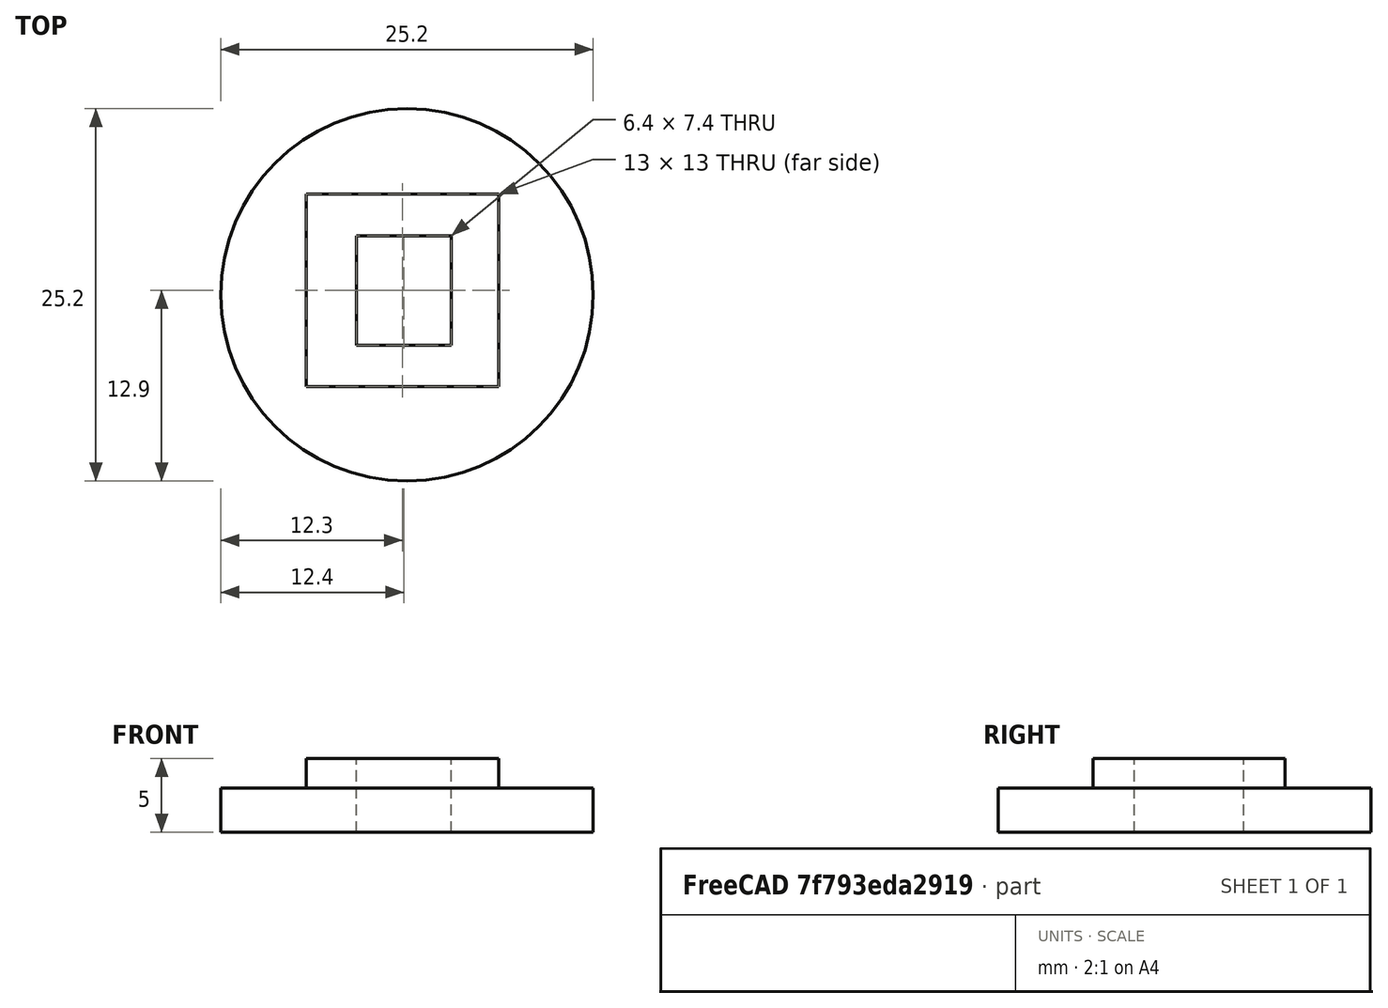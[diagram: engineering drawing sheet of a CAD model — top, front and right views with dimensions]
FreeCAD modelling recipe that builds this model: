
FCSTD DOCUMENT  (FreeCAD 0.21R33668 +26 (Git))
Label: fibre_holder
License: All rights reserved
LicenseURL: http://en.wikipedia.org/wiki/All_rights_reserved
objects: Part::Cylinder×4, Part::Box×2, Part::Cut×2, Part::MultiFuse×1, Part::MultiCommon×1
note: 10 computed .brp shape members not serialized (recipe doc carries the construction recipe); baked Part::Feature solids carry a one-line shape summary decoded from their .brp

FEATURE [Part::Box] Box  label="Cube"
  AttacherType = Attacher::AttachEngine3D
  Height = 10
  Length = 6.4
  Width = 7.4
FEATURE [Part::Cylinder] Cylinder
  Angle = 360
  AttacherType = Attacher::AttachEngine3D
  FirstAngle = 0
  Height = 10
  Placement = pos=(3.2,3.5,0) rot=(0,0,1;0rad)
  Radius = 17.4
  SecondAngle = 0
FEATURE [Part::Cylinder] Cylinder001
  Angle = 360
  AttacherType = Attacher::AttachEngine3D
  FirstAngle = 0
  Height = 12
  Placement = pos=(3.2,3.5,0) rot=(0,0,1;0rad)
  Radius = 14.4
  SecondAngle = 0
FEATURE [Part::Cylinder] Cylinder002
  Angle = 360
  AttacherType = Attacher::AttachEngine3D
  FirstAngle = 0
  Height = 3
  Placement = pos=(3.2,3.5,0) rot=(0,0,1;0rad)
  Radius = 15.4
  SecondAngle = 0
FEATURE [Part::Cut] Cut
  Base = -> Cylinder
  Tool = -> Cylinder001
FEATURE [Part::Box] Box001  label="Cube001"
  AttacherType = Attacher::AttachEngine3D
  Height = 5
  Length = 13
  Placement = pos=(-3.4,-2.8,0) rot=(0,0,1;0rad)
  Width = 13
FEATURE [Part::MultiFuse] Fusion
  Shapes = -> [Box001,Cylinder002,Cut]
FEATURE [Part::Cut] Cut001
  Base = -> Fusion
  Tool = -> Box
FEATURE [Part::Cylinder] Cylinder003
  Angle = 360
  AttacherType = Attacher::AttachEngine3D
  FirstAngle = 0
  Height = 17
  Placement = pos=(3.4,3.4,-6) rot=(0,0,1;0rad)
  Radius = 12.6
  SecondAngle = 0
FEATURE [Part::MultiCommon] Common
  Shapes = -> [Cut001,Cylinder003]
